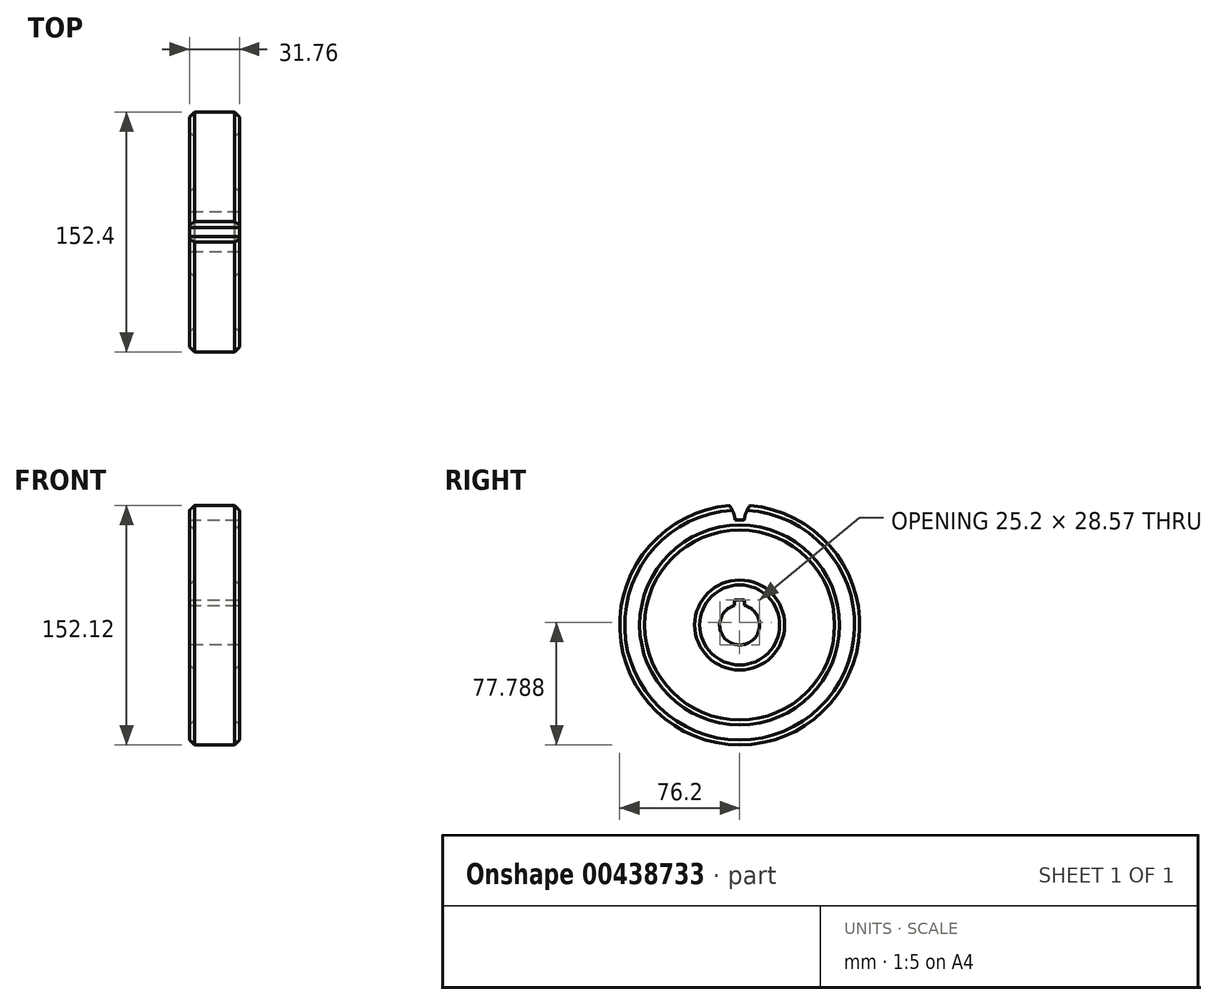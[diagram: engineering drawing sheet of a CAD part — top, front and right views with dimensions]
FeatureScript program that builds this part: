
annotation { "Feature Type Name" : "Feature", "Feature Type Description" : "" }
export const myFeature = defineFeature(function(context is Context, id is Id, definition is map)
    precondition{}
    {
        {
            var Q0;
            Q0=qCreatedBy(makeId("Front.planeOp"),FACE);
            var sketch = newSketch(context, id + "F0", { "sketchPlane" : qUnion([Q0])});
            skLineSegment(sketch, "E0", {"start": v(0, 0) * mm, "end": v(0, 63.5) * mm});
            skLineSegment(sketch, "E1", {"start": v(0, 63.5) * mm, "end": v(12.7, 63.5) * mm});
            skLineSegment(sketch, "E2", {"start": v(12.7, 63.5) * mm, "end": v(15.88, 60.32) * mm});
            skLineSegment(sketch, "E3", {"start": v(15.87, 60.32) * mm, "end": v(15.87, 50.8) * mm});
            skLineSegment(sketch, "E4", {"start": v(15.88, 50.8) * mm, "end": v(12.7, 47.62) * mm});
            skLineSegment(sketch, "E5", {"start": v(12.7, 47.62) * mm, "end": v(12.7, 15.88) * mm});
            skLineSegment(sketch, "E6", {"start": v(12.7, 15.88) * mm, "end": v(15.88, 12.7) * mm});
            skLineSegment(sketch, "E7", {"start": v(15.88, 12.7) * mm, "end": v(15.88, 0) * mm});
            skLineSegment(sketch, "E8", {"start": v(15.88, 0) * mm, "end": v(0, 0) * mm});
            skLineSegment(sketch, "E9", {"start": v(0, 0) * mm, "end": v(0, -12.7) * mm});
            skLineSegment(sketch, "E10", {"start": v(0, -12.7) * mm, "end": v(7.64, -12.7) * mm});
            skLineSegment(sketch, "E11.MirrorCS", {"start": v(0, 63.5) * mm, "end": v(-12.7, 63.5) * mm});
            skLineSegment(sketch, "E12.MirrorCS", {"start": v(-12.7, 63.5) * mm, "end": v(-15.88, 60.32) * mm});
            skLineSegment(sketch, "E13.MirrorCS", {"start": v(-15.88, 60.32) * mm, "end": v(-15.88, 50.8) * mm});
            skLineSegment(sketch, "E14.MirrorCS", {"start": v(-12.7, 47.62) * mm, "end": v(-12.7, 15.88) * mm});
            skLineSegment(sketch, "E15.MirrorCS", {"start": v(-15.88, 50.8) * mm, "end": v(-12.7, 47.62) * mm});
            skLineSegment(sketch, "E16.MirrorCS", {"start": v(-12.7, 15.88) * mm, "end": v(-15.88, 12.7) * mm});
            skLineSegment(sketch, "E17.MirrorCS", {"start": v(-15.88, 12.7) * mm, "end": v(-15.88, 0) * mm});
            skLineSegment(sketch, "E18.MirrorCS", {"start": v(-15.88, 0) * mm, "end": v(0, 0) * mm});
            skSolve(sketch);
        }
        {
            var Q0;
            Q0=makeQuery(id+"F0.imprint","IMPRINT",FACE,{"disambiguationData":[TD([[makeQuery(id+"F0.imprint","IMPRINT",EDGE,{"derivedFrom":sQuery(id+"F0.wireOp",EDGE,"E0")}),-1.0]])]});
            var Q1;
            Q1=makeQuery(id+"F0.imprint","IMPRINT",FACE,{"disambiguationData":[TD([[makeQuery(id+"F0.imprint","IMPRINT",EDGE,{"derivedFrom":sQuery(id+"F0.wireOp",EDGE,"E0")}),1.0]])]});
            var Q2;
            Q2=sQuery(id+"F0.wireOp",EDGE,"E10");
            revolve(context, id + "F1", {"entities" : qUnion([Q0, Q1]), "axis" : qUnion([Q2]), "revolveType" : RevolveType.FULL});
        }
        {
            var Q0;
            Q0=makeQuery(id+"F1.opRevolve","SWEPT_FACE",FACE,{"disambiguationData":[OSD([sQuery(id+"F0.wireOp",EDGE,"E3")])]});
            var sketch = newSketch(context, id + "F2", { "sketchPlane" : qUnion([Q0])});
            skLineSegment(sketch, "E19", {"start": v(0, -12.7) * mm, "end": v(0, 120.65) * mm});
            skLineSegment(sketch, "E20", {"start": v(0, 53.98) * mm, "end": v(2.86, 53.98) * mm});
            skPoint(sketch, "E20.endSnap0", {"position": v(0, 53.98) * mm});
            skArc(sketch, "E21", {"start": v(6.54, 63.22) * mm, "mid": v(4.08, 58.84) * mm, "end": v(2.86, 53.98) * mm});
            skLineSegment(sketch, "E22.MirrorCS", {"start": v(0, 53.98) * mm, "end": v(-2.86, 53.98) * mm});
            skArc(sketch, "E23.MirrorCS", {"start": v(-6.54, 63.22) * mm, "mid": v(-4.08, 58.84) * mm, "end": v(-2.86, 53.98) * mm});
            skArc(sketch, "E24.0", {"start": v(6.54, 63.22) * mm, "mid": v(0, 63.5) * mm, "end": v(-6.54, 63.22) * mm});
            skSolve(sketch);
        }
        {
            var Q0;
            {var subQ0=sQuery(id+"F2.wireOp",EDGE,"E24.0");var subQ5=sQuery(id+"F2.wireOp",EDGE,"E23.MirrorCS");var subQ6=makeQuery(id+"F2.imprint","INTERSECT",VERTEX,{"derivedFrom":[subQ5,subQ0]});Q0=makeQuery(id+"F2.imprint","IMPRINT",FACE,{"disambiguationData":[TD([[makeQuery(id+"F2.imprint","IMPRINT",EDGE,{"disambiguationData":[TD([[subQ6,1.0]])],"derivedFrom":subQ0}),1.0]])]});}
            var Q1;
            {var subQ0=sQuery(id+"F2.wireOp",EDGE,"E22.MirrorCS");Q1=makeQuery(id+"F2.imprint","IMPRINT",FACE,{"disambiguationData":[TD([[makeQuery(id+"F2.imprint","IMPRINT",EDGE,{"derivedFrom":subQ0}),-1.0]])]});}
            var Q2;
            {var subQ0=sQuery(id+"F2.wireOp",EDGE,"E20");Q2=makeQuery(id+"F2.imprint","IMPRINT",FACE,{"disambiguationData":[TD([[makeQuery(id+"F2.imprint","IMPRINT",EDGE,{"derivedFrom":subQ0}),1.0]])]});}
            var Q3;
            {var subQ0=sQuery(id+"F2.wireOp",EDGE,"E24.0");var subQ5=sQuery(id+"F2.wireOp",EDGE,"E21");var subQ6=makeQuery(id+"F2.imprint","INTERSECT",VERTEX,{"derivedFrom":[subQ5,subQ0]});Q3=makeQuery(id+"F2.imprint","IMPRINT",FACE,{"disambiguationData":[TD([[makeQuery(id+"F2.imprint","IMPRINT",EDGE,{"disambiguationData":[TD([[subQ6,-1.0]])],"derivedFrom":subQ0}),1.0]])]});}
            extrude(context, id + "F3", {"entities" : qUnion([Q0, Q1, Q2, Q3]), "operationType" : NewBodyOperationType.REMOVE, "endBound" : BoundingType.THROUGH_ALL, "oppositeDirection" : true, "depth" : 25.4 * mm});
        }
        {
            var Q0;
            Q0=makeQuery(id+"F1.opRevolve","SWEPT_FACE",FACE,{"disambiguationData":[OSD([sQuery(id+"F0.wireOp",EDGE,"E7")])]});
            var sketch = newSketch(context, id + "F4", { "sketchPlane" : qUnion([Q0])});
            skLineSegment(sketch, "E25", {"start": v(0, -12.7) * mm, "end": v(0, 78.13) * mm});
            skLineSegment(sketch, "E26", {"start": v(0, 3.17) * mm, "end": v(3.18, 3.17) * mm});
            skLineSegment(sketch, "E27", {"start": v(3.17, 3.18) * mm, "end": v(3.17, -0.4) * mm});
            skLineSegment(sketch, "E28.MirrorCS", {"start": v(0, 3.17) * mm, "end": v(-3.18, 3.17) * mm});
            skLineSegment(sketch, "E29.MirrorCS", {"start": v(-3.18, 3.18) * mm, "end": v(-3.18, -0.4) * mm});
            skArc(sketch, "E30.0", {"start": v(3.17, -0.4) * mm, "mid": v(0, 0) * mm, "end": v(-3.17, -0.4) * mm});
            skSolve(sketch);
        }
        {
            var Q0;
            {var subQ0=sQuery(id+"F4.wireOp",EDGE,"E26");Q0=makeQuery(id+"F4.imprint","IMPRINT",FACE,{"disambiguationData":[TD([[makeQuery(id+"F4.imprint","IMPRINT",EDGE,{"derivedFrom":subQ0}),-1.0]])]});}
            var Q1;
            {var subQ0=sQuery(id+"F4.wireOp",EDGE,"E28.MirrorCS");Q1=makeQuery(id+"F4.imprint","IMPRINT",FACE,{"disambiguationData":[TD([[makeQuery(id+"F4.imprint","IMPRINT",EDGE,{"derivedFrom":subQ0}),1.0]])]});}
            extrude(context, id + "F5", {"entities" : qUnion([Q0, Q1]), "operationType" : NewBodyOperationType.REMOVE, "endBound" : BoundingType.THROUGH_ALL, "oppositeDirection" : true, "depth" : 25.4 * mm});
        }
    });
